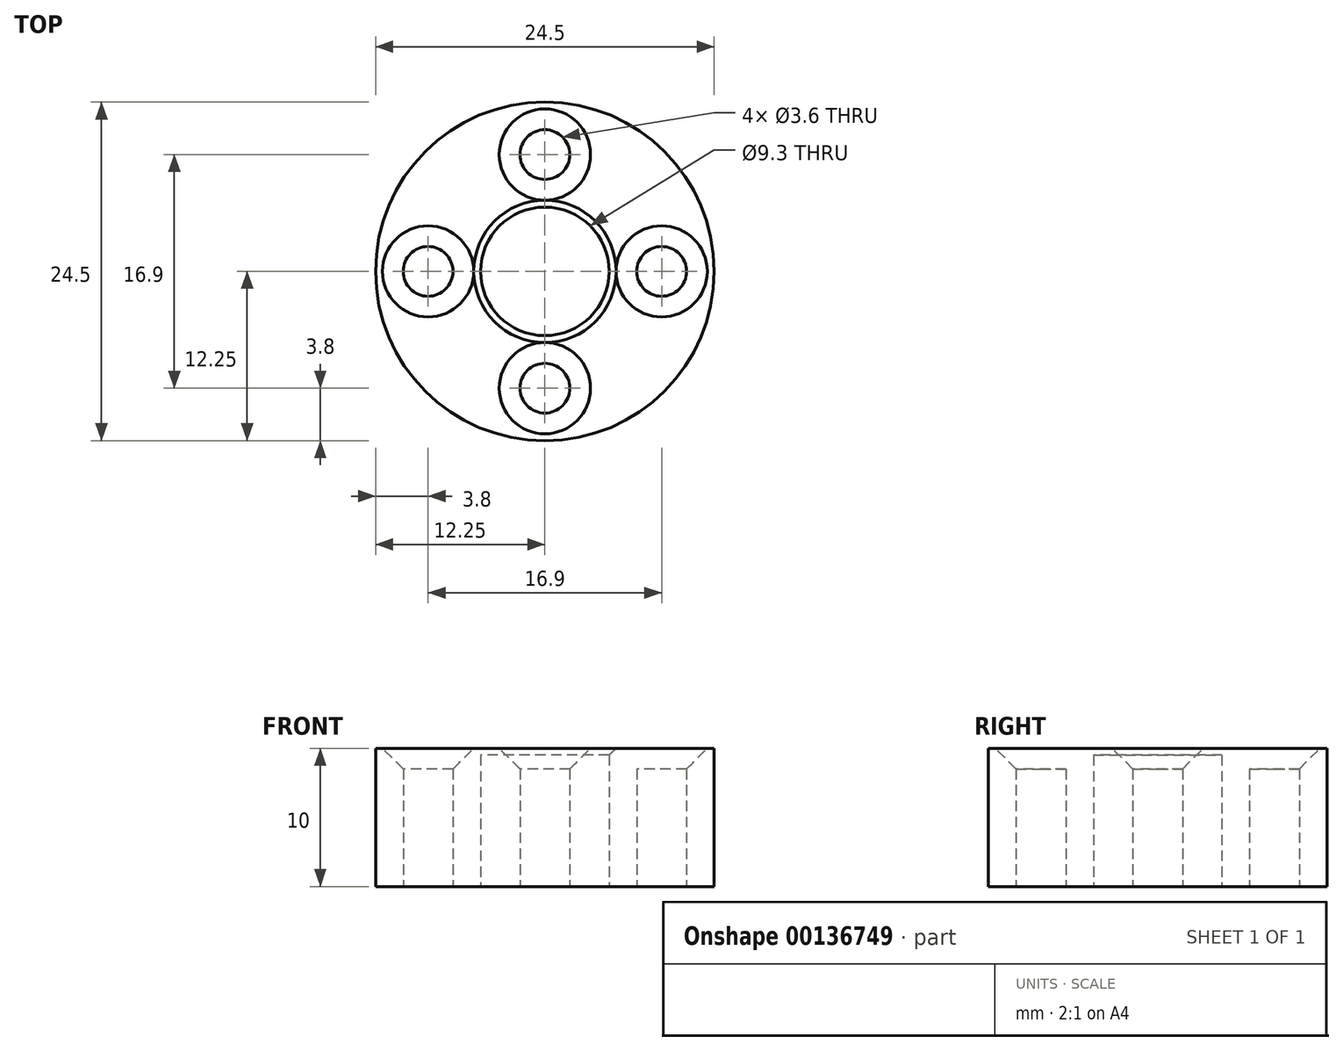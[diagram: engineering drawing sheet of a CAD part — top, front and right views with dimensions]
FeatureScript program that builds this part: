
annotation { "Feature Type Name" : "Feature", "Feature Type Description" : "" }
export const myFeature = defineFeature(function(context is Context, id is Id, definition is map)
    precondition{}
    {
        {
            var Q0;
            Q0=qCreatedBy(makeId("Top.planeOp"),FACE);
            var sketch = newSketch(context, id + "F0", { "sketchPlane" : qUnion([Q0])});
            skCircle(sketch, "E0", {"center": v(0, 0) * mm, "radius": 12.25 * mm});
            skCircle(sketch, "E1", {"center": v(0, 0) * mm, "radius": 4.65 * mm});
            skCircle(sketch, "E2", {"center": v(8.45, 0) * mm, "radius": 1.8 * mm});
            skCircle(sketch, "E3.1.0", {"center": v(0, 8.45) * mm, "radius": 1.8 * mm});
            skCircle(sketch, "E3.2.0", {"center": v(-8.45, 0) * mm, "radius": 1.8 * mm});
            skCircle(sketch, "E3.3.0", {"center": v(0, -8.45) * mm, "radius": 1.8 * mm});
            skSolve(sketch);
        }
        {
            var Q0;
            Q0=makeQuery(id+"F0.imprint","IMPRINT",FACE,{"disambiguationData":[TD([[makeQuery(id+"F0.imprint","IMPRINT",EDGE,{"derivedFrom":sQuery(id+"F0.wireOp",EDGE,"E0")}),1.0]])]});
            extrude(context, id + "F1", {"entities" : qUnion([Q0]), "depth" : 10 * mm, "offsetDistance" : 25 * mm});
        }
        {
            var Q0;
            Q0=makeQuery(id+"F1.opExtrude","CAP_EDGE",EDGE,{"disambiguationData":[OSD([sQuery(id+"F0.wireOp",EDGE,"E3.2.0")])],"isStart":false});
            var Q1;
            Q1=makeQuery(id+"F1.opExtrude","CAP_EDGE",EDGE,{"disambiguationData":[OSD([sQuery(id+"F0.wireOp",EDGE,"E3.1.0")])],"isStart":false});
            var Q2;
            Q2=makeQuery(id+"F1.opExtrude","CAP_EDGE",EDGE,{"disambiguationData":[OSD([sQuery(id+"F0.wireOp",EDGE,"E2")])],"isStart":false});
            var Q3;
            Q3=makeQuery(id+"F1.opExtrude","CAP_EDGE",EDGE,{"disambiguationData":[OSD([sQuery(id+"F0.wireOp",EDGE,"E3.3.0")])],"isStart":false});
            chamfer(context, id + "F2", {"entities" : qUnion([Q0, Q1, Q2, Q3]), "width" : 1.5 * mm, "tangentPropagation" : true});
        }
        {
            var Q0;
            Q0=makeQuery(id+"F1.opExtrude","CAP_EDGE",EDGE,{"disambiguationData":[OSD([sQuery(id+"F0.wireOp",EDGE,"E1")])],"isStart":false});
            chamfer(context, id + "F3", {"entities" : qUnion([Q0]), "width" : 0.5 * mm, "tangentPropagation" : true});
        }
    });
